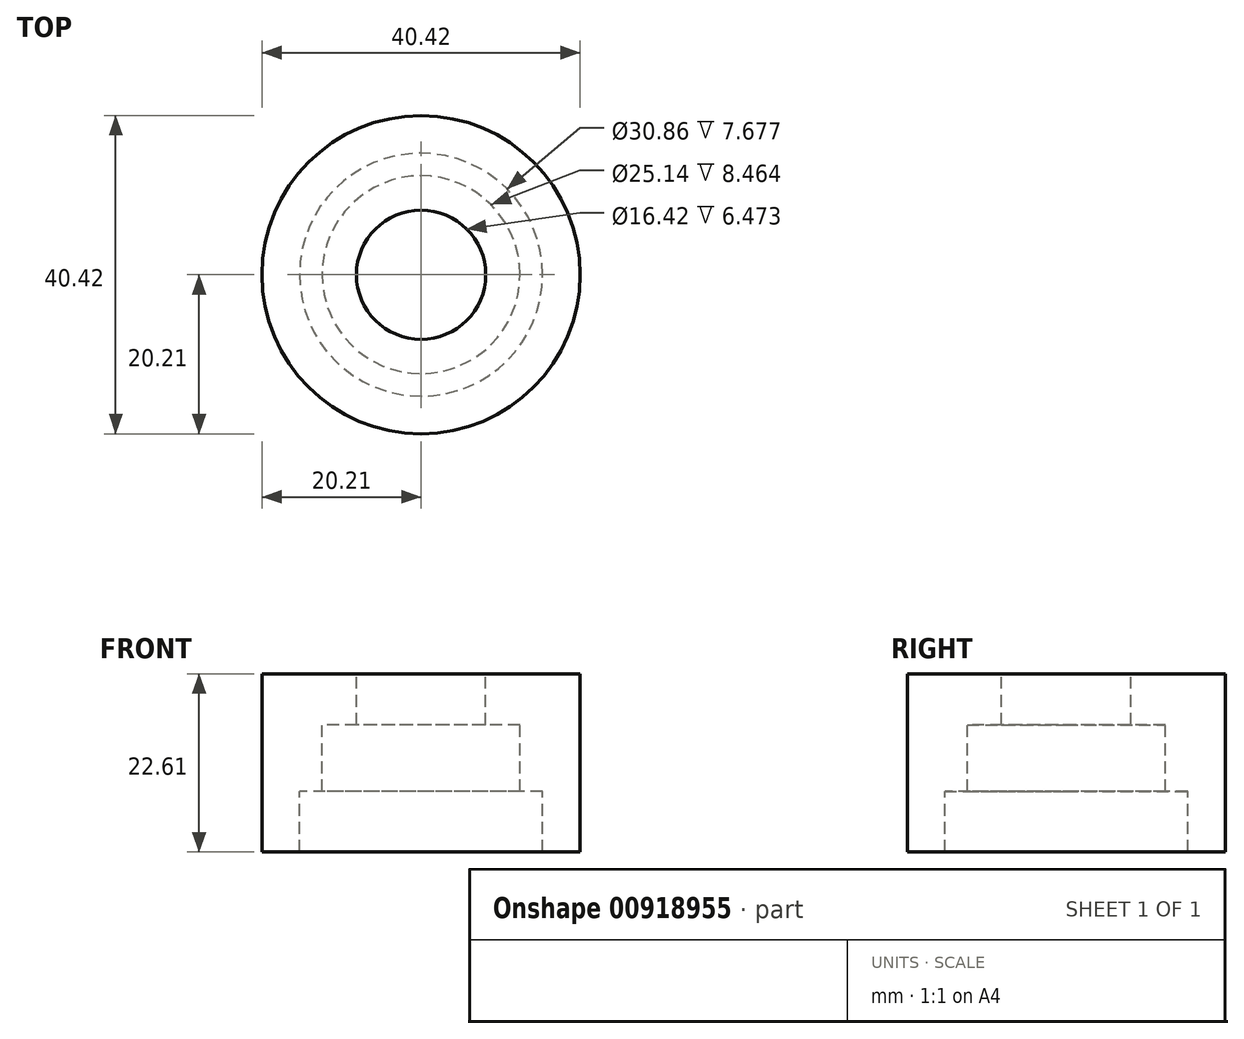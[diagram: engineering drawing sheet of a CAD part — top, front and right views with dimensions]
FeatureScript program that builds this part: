
annotation { "Feature Type Name" : "Feature", "Feature Type Description" : "" }
export const myFeature = defineFeature(function(context is Context, id is Id, definition is map)
    precondition{}
    {
        {
            var Q0;
            Q0=qCreatedBy(makeId("Front.planeOp"),FACE);
            var sketch = newSketch(context, id + "F0", { "sketchPlane" : qUnion([Q0])});
            skLineSegment(sketch, "E0", {"start": v(0, 22.61) * mm, "end": v(0, 0) * mm, "construction": true});
            skLineSegment(sketch, "E1", {"start": v(-15.43, 0) * mm, "end": v(-20.2, 0) * mm});
            skLineSegment(sketch, "E2", {"start": v(-20.2, 0) * mm, "end": v(-20.2, 22.61) * mm});
            skLineSegment(sketch, "E3", {"start": v(-20.2, 22.61) * mm, "end": v(-8.21, 22.61) * mm});
            skLineSegment(sketch, "E4", {"start": v(-8.21, 22.61) * mm, "end": v(-8.21, 16.14) * mm});
            skLineSegment(sketch, "E5", {"start": v(-8.21, 16.14) * mm, "end": v(-12.57, 16.14) * mm});
            skLineSegment(sketch, "E6", {"start": v(-12.57, 16.14) * mm, "end": v(-12.57, 7.68) * mm});
            skLineSegment(sketch, "E7", {"start": v(-12.57, 7.68) * mm, "end": v(-15.43, 7.68) * mm});
            skLineSegment(sketch, "E8", {"start": v(-15.43, 7.68) * mm, "end": v(-15.43, 0) * mm});
            skSolve(sketch);
        }
        {
            var Q0;
            Q0=makeQuery(id+"F0.imprint","IMPRINT",FACE,{"disambiguationData":[TD([[makeQuery(id+"F0.imprint","IMPRINT",EDGE,{"derivedFrom":sQuery(id+"F0.wireOp",EDGE,"E1")}),-1.0]])]});
            var Q1;
            Q1=sQuery(id+"F0.wireOp",EDGE,"E0");
            revolve(context, id + "F1", {"surfaceOperationType" : NewSurfaceOperationType.NEW, "entities" : qUnion([Q0]), "axis" : qUnion([Q1]), "revolveType" : RevolveType.FULL});
        }
    });
